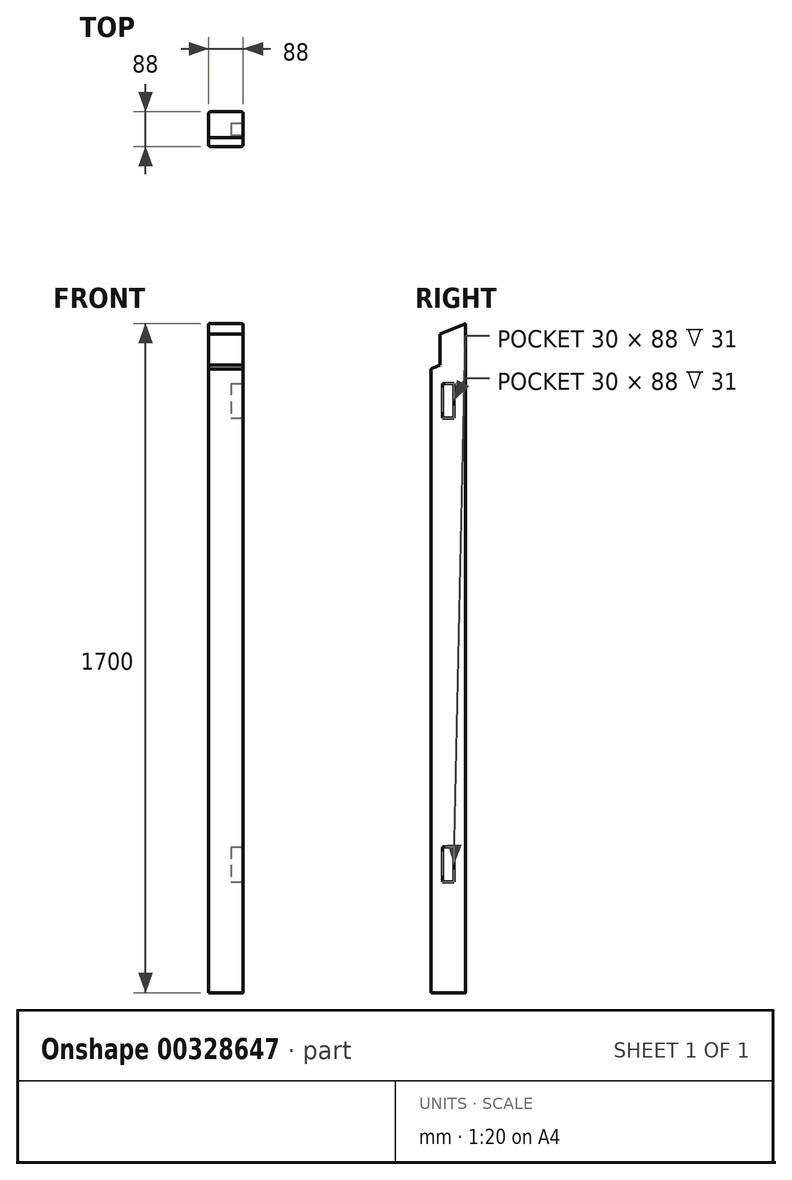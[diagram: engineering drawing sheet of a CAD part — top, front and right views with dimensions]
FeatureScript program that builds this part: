
annotation { "Feature Type Name" : "Feature", "Feature Type Description" : "" }
export const myFeature = defineFeature(function(context is Context, id is Id, definition is map)
    precondition{}
    {
        {
            var Q0;
            Q0=qCreatedBy(makeId("Top.planeOp"),FACE);
            var sketch = newSketch(context, id + "F0", { "sketchPlane" : qUnion([Q0])});
            skLineSegment(sketch, "E0.bottom", {"start": v(0, 0) * mm, "end": v(88, 0) * mm});
            skLineSegment(sketch, "E0.top", {"start": v(0, 88) * mm, "end": v(88, 88) * mm});
            skLineSegment(sketch, "E0.left", {"start": v(0, 0) * mm, "end": v(0, 88) * mm});
            skLineSegment(sketch, "E0.right", {"start": v(88, 0) * mm, "end": v(88, 88) * mm});
            skSolve(sketch);
        }
        {
            var Q0;
            Q0=qSketchRegion(id+"F0",true);
            extrude(context, id + "F1", {"entities" : qUnion([Q0]), "depth" : 1700 * mm});
        }
        {
            var Q0;
            Q0=makeQuery(id+"F1.opExtrude","SWEPT_FACE",FACE,{"disambiguationData":[OSD([sQuery(id+"F0.wireOp",EDGE,"E0.right")])]});
            var sketch = newSketch(context, id + "F2", { "sketchPlane" : qUnion([Q0])});
            skLineSegment(sketch, "E1", {"start": v(44, 0) * mm, "end": v(44, 282) * mm, "construction": true});
            skPoint(sketch, "E1.endSnap0", {"position": v(44, 0) * mm});
            skLineSegment(sketch, "E2", {"start": v(44, 282) * mm, "end": v(29, 282) * mm});
            skLineSegment(sketch, "E3", {"start": v(29, 282) * mm, "end": v(29, 370) * mm});
            skLineSegment(sketch, "E4", {"start": v(29, 370) * mm, "end": v(59, 370) * mm});
            skLineSegment(sketch, "E5", {"start": v(59, 370) * mm, "end": v(59, 282) * mm});
            skLineSegment(sketch, "E6", {"start": v(59, 282) * mm, "end": v(44, 282) * mm});
            skSolve(sketch);
        }
        {
            var Q0;
            Q0=qSketchRegion(id+"F2",true);
            extrude(context, id + "F3", {"entities" : qUnion([Q0]), "operationType" : NewBodyOperationType.REMOVE, "oppositeDirection" : true, "depth" : 31 * mm});
        }
        {
            var Q0;
            Q0=makeQuery(id+"F1.opExtrude","SWEPT_FACE",FACE,{"disambiguationData":[OSD([sQuery(id+"F0.wireOp",EDGE,"E0.right")])]});
            var sketch = newSketch(context, id + "F4", { "sketchPlane" : qUnion([Q0])});
            skLineSegment(sketch, "E7", {"start": v(44, 0) * mm, "end": v(44, 1460) * mm, "construction": true});
            skPoint(sketch, "E7.endSnap0", {"position": v(44, 370) * mm});
            skLineSegment(sketch, "E8", {"start": v(44, 1460) * mm, "end": v(29, 1460) * mm});
            skLineSegment(sketch, "E9", {"start": v(29, 1460) * mm, "end": v(29, 1548) * mm});
            skLineSegment(sketch, "E10", {"start": v(29, 1548) * mm, "end": v(59, 1548) * mm});
            skLineSegment(sketch, "E11", {"start": v(59, 1548) * mm, "end": v(59, 1460) * mm});
            skLineSegment(sketch, "E12", {"start": v(59, 1460) * mm, "end": v(44, 1460) * mm});
            skSolve(sketch);
        }
        {
            var Q0;
            Q0=qSketchRegion(id+"F4",true);
            extrude(context, id + "F5", {"entities" : qUnion([Q0]), "operationType" : NewBodyOperationType.REMOVE, "oppositeDirection" : true, "depth" : 31 * mm});
        }
        {
            var Q0;
            Q0=makeQuery(id+"F1.opExtrude","SWEPT_FACE",FACE,{"disambiguationData":[OSD([sQuery(id+"F0.wireOp",EDGE,"E0.right")])]});
            var sketch = newSketch(context, id + "F6", { "sketchPlane" : qUnion([Q0])});
            skLineSegment(sketch, "E13", {"start": v(88, 1700) * mm, "end": v(0, 1663.55) * mm});
            skLineSegment(sketch, "E14", {"start": v(0, 1663.55) * mm, "end": v(0, 1700) * mm});
            skLineSegment(sketch, "E15", {"start": v(0, 1700) * mm, "end": v(88, 1700) * mm});
            skSolve(sketch);
        }
        {
            var Q0;
            Q0=qSketchRegion(id+"F6",true);
            extrude(context, id + "F7", {"entities" : qUnion([Q0]), "operationType" : NewBodyOperationType.REMOVE, "endBound" : BoundingType.THROUGH_ALL, "oppositeDirection" : true, "depth" : 260.2 * mm});
        }
        {
            var Q0;
            Q0=makeQuery(id+"F1.opExtrude","SWEPT_FACE",FACE,{"disambiguationData":[OSD([sQuery(id+"F0.wireOp",EDGE,"E0.right")])]});
            var sketch = newSketch(context, id + "F8", { "sketchPlane" : qUnion([Q0])});
            skLineSegment(sketch, "E16", {"start": v(23, 1673.08) * mm, "end": v(23, 1594.08) * mm});
            skLineSegment(sketch, "E17", {"start": v(0, 1663.55) * mm, "end": v(23, 1673.08) * mm});
            skLineSegment(sketch, "E18", {"start": v(23, 1594.08) * mm, "end": v(0, 1584.55) * mm});
            skPoint(sketch, "E19.end.orphan", {"position": v(0, 1608.54) * mm});
            skLineSegment(sketch, "E20", {"start": v(0, 1663.55) * mm, "end": v(0, 1584.55) * mm});
            skSolve(sketch);
        }
        {
            var Q0;
            Q0=makeQuery(id+"F8.imprint","IMPRINT",FACE,{"disambiguationData":[TD([[makeQuery(id+"F8.imprint","IMPRINT",EDGE,{"derivedFrom":sQuery(id+"F8.wireOp",EDGE,"E16")}),-1.0]])]});
            extrude(context, id + "F9", {"entities" : qUnion([Q0]), "operationType" : NewBodyOperationType.REMOVE, "endBound" : BoundingType.THROUGH_ALL, "oppositeDirection" : true, "depth" : 204.57 * mm});
        }
        {
            var Q0;
            Q0=makeQuery(id+"F1.opExtrude","SWEPT_EDGE",EDGE,{"disambiguationData":[OSD([sQuery(id+"F0.wireOp",EDGE,"E0.bottom"),sQuery(id+"F0.wireOp",EDGE,"E0.left")])]});
            var Q1;
            Q1=makeQuery(id+"F1.opExtrude","SWEPT_EDGE",EDGE,{"disambiguationData":[OSD([sQuery(id+"F0.wireOp",EDGE,"E0.bottom"),sQuery(id+"F0.wireOp",EDGE,"E0.right")])]});
            var Q2;
            Q2=makeQuery(id+"F1.opExtrude","SWEPT_EDGE",EDGE,{"disambiguationData":[OSD([sQuery(id+"F0.wireOp",EDGE,"E0.top"),sQuery(id+"F0.wireOp",EDGE,"E0.right")])]});
            var Q3;
            Q3=makeQuery(id+"F1.opExtrude","SWEPT_EDGE",EDGE,{"disambiguationData":[OSD([sQuery(id+"F0.wireOp",EDGE,"E0.top"),sQuery(id+"F0.wireOp",EDGE,"E0.left")])]});
            fillet(context, id + "F10", {"entities" : qUnion([Q0, Q1, Q2, Q3]), "radius" : 5 * mm, "tangentPropagation" : true, "allowEdgeOverflow" : false});
        }
    });
